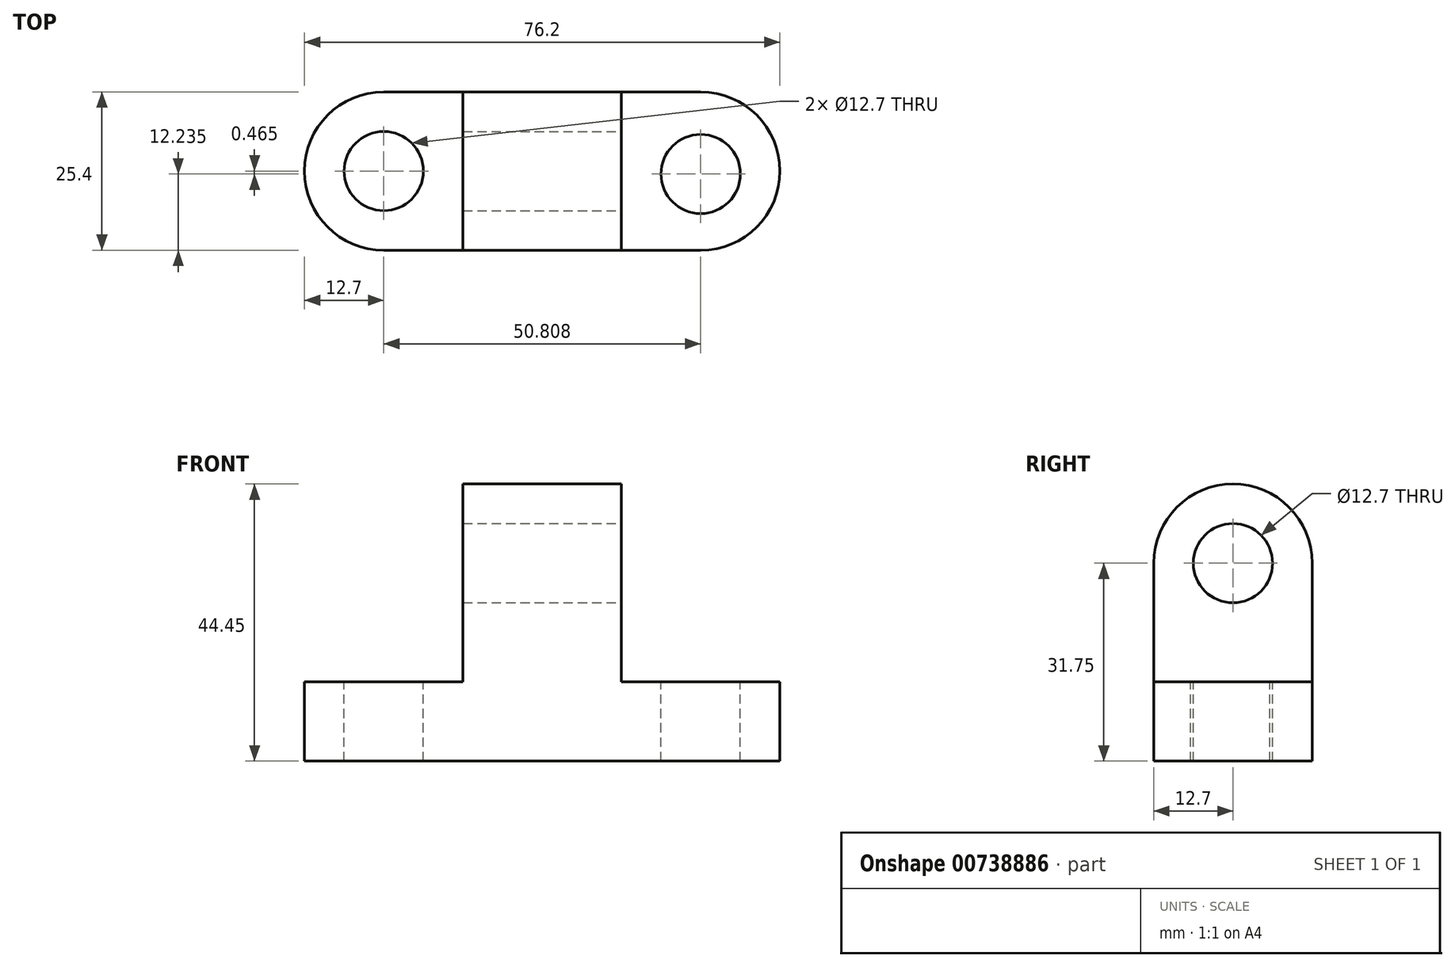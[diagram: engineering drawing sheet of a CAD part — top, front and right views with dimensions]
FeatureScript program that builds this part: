
annotation { "Feature Type Name" : "Feature", "Feature Type Description" : "" }
export const myFeature = defineFeature(function(context is Context, id is Id, definition is map)
    precondition{}
    {
        {
            var Q0;
            Q0=qCreatedBy(makeId("Front.planeOp"),FACE);
            var sketch = newSketch(context, id + "F0", { "sketchPlane" : qUnion([Q0])});
            skLineSegment(sketch, "E0", {"start": v(0, 0) * mm, "end": v(0, 44.45) * mm});
            skLineSegment(sketch, "E1", {"start": v(0, 44.45) * mm, "end": v(76.2, 44.45) * mm});
            skLineSegment(sketch, "E2", {"start": v(76.2, 44.45) * mm, "end": v(76.2, 0) * mm});
            skLineSegment(sketch, "E3", {"start": v(76.2, 0) * mm, "end": v(0, 0) * mm});
            skSolve(sketch);
        }
        {
            var Q0;
            Q0 = qSketchRegion(id + "F0", true);
            extrude(context, id + "F1", {"entities" : qUnion([Q0]), "depth" : 25.4 * mm, "offsetDistance" : 25.4 * mm});
        }
        {
            var Q0;
            Q0=makeQuery(id+"F1.opExtrude","CAP_FACE",FACE,{"disambiguationData":[OSD([sQuery(id+"F0.wireOp",EDGE,"E0"),sQuery(id+"F0.wireOp",EDGE,"E1"),sQuery(id+"F0.wireOp",EDGE,"E2"),sQuery(id+"F0.wireOp",EDGE,"E3")])],"isStart":false});
            var sketch = newSketch(context, id + "F2", { "sketchPlane" : qUnion([Q0])});
            skLineSegment(sketch, "E4", {"start": v(50.8, 44.45) * mm, "end": v(50.8, 12.7) * mm});
            skLineSegment(sketch, "E5", {"start": v(50.8, 12.7) * mm, "end": v(76.2, 12.7) * mm});
            skLineSegment(sketch, "E6", {"start": v(25.4, 44.45) * mm, "end": v(25.4, 12.7) * mm});
            skLineSegment(sketch, "E7", {"start": v(25.4, 12.7) * mm, "end": v(0, 12.7) * mm});
            skSolve(sketch);
        }
        {
            var Q0;
            Q0 = qSketchRegion(id + "F2", true);
            var Q1;
            {var subQ0=sQuery(id+"F2.wireOp",EDGE,"E6");Q1=makeQuery(id+"F2.imprint","IMPRINT",FACE,{"disambiguationData":[TD([[makeQuery(id+"F2.imprint","IMPRINT",EDGE,{"derivedFrom":subQ0}),-1.0]])]});}
            var Q2;
            {var subQ0=sQuery(id+"F2.wireOp",EDGE,"E4");Q2=makeQuery(id+"F2.imprint","IMPRINT",FACE,{"disambiguationData":[TD([[makeQuery(id+"F2.imprint","IMPRINT",EDGE,{"derivedFrom":subQ0}),1.0]])]});}
            extrude(context, id + "F3", {"entities" : qUnion([Q0, Q1, Q2]), "operationType" : NewBodyOperationType.REMOVE, "oppositeDirection" : true, "depth" : 25.4 * mm, "offsetDistance" : 25.4 * mm});
        }
        {
            var Q0;
            Q0=makeQuery(id+"F3.boolean.opBoolean","COPY",FACE,{"derivedFrom":makeQuery(id+"F3.opExtrude","SWEPT_FACE",FACE,{"disambiguationData":[OSD([sQuery(id+"F2.wireOp",EDGE,"E4")])]})});
            var sketch = newSketch(context, id + "F4", { "sketchPlane" : qUnion([Q0])});
            skCircle(sketch, "E8", {"center": v(-12.7, 31.75) * mm, "radius": 6.35 * mm});
            skArc(sketch, "E9", {"start": v(0, 31.75) * mm, "mid": v(-12.7, 44.45) * mm, "end": v(-25.4, 31.75) * mm});
            skSolve(sketch);
        }
        {
            var Q0;
            Q0 = qSketchRegion(id + "F4", true);
            var Q1;
            {var subQ0=sQuery(id+"F4.wireOp",EDGE,"E9");var subQ1=sQuery(id+"F2.wireOp",EDGE,"E4");var subQ2=makeQuery(id+"F3.boolean.opBoolean","COPY",EDGE,{"derivedFrom":makeQuery(id+"F3.opExtrude","CAP_EDGE",EDGE,{"disambiguationData":[OSD([subQ1])],"isStart":false})});var subQ3=makeQuery(id+"F4.imprint","INTERSECT",VERTEX,{"derivedFrom":[subQ2,subQ0]});Q1=makeQuery(id+"F4.imprint","IMPRINT",FACE,{"disambiguationData":[TD([[makeQuery(id+"F4.imprint","IMPRINT",EDGE,{"disambiguationData":[TD([[subQ3,-1.0]])],"derivedFrom":subQ0}),-1.0]])]});}
            var Q2;
            {var subQ0=sQuery(id+"F4.wireOp",EDGE,"E9");var subQ1=sQuery(id+"F2.wireOp",EDGE,"E4");var subQ2=makeQuery(id+"F3.boolean.opBoolean","COPY",EDGE,{"derivedFrom":makeQuery(id+"F3.opExtrude","CAP_EDGE",EDGE,{"disambiguationData":[OSD([subQ1])],"isStart":true})});var subQ3=makeQuery(id+"F4.imprint","INTERSECT",VERTEX,{"derivedFrom":[subQ2,subQ0]});Q2=makeQuery(id+"F4.imprint","IMPRINT",FACE,{"disambiguationData":[TD([[makeQuery(id+"F4.imprint","IMPRINT",EDGE,{"disambiguationData":[TD([[subQ3,1.0]])],"derivedFrom":subQ0}),-1.0]])]});}
            extrude(context, id + "F5", {"entities" : qUnion([Q0, Q1, Q2]), "operationType" : NewBodyOperationType.REMOVE, "oppositeDirection" : true, "depth" : 25.4 * mm, "offsetDistance" : 25.4 * mm});
        }
        {
            var Q0;
            Q0=makeQuery(id+"F3.boolean.opBoolean","COPY",FACE,{"derivedFrom":makeQuery(id+"F3.opExtrude","SWEPT_FACE",FACE,{"disambiguationData":[OSD([sQuery(id+"F2.wireOp",EDGE,"E7")])]})});
            var sketch = newSketch(context, id + "F6", { "sketchPlane" : qUnion([Q0])});
            skCircle(sketch, "E10", {"center": v(12.7, -12.7) * mm, "radius": 6.35 * mm});
            skArc(sketch, "E11", {"start": v(12.7, 0) * mm, "mid": v(0, -12.7) * mm, "end": v(12.7, -25.4) * mm});
            skSolve(sketch);
        }
        {
            var Q0;
            Q0=makeQuery(id+"F6.imprint","IMPRINT",FACE,{"disambiguationData":[TD([[makeQuery(id+"F6.imprint","IMPRINT",EDGE,{"derivedFrom":sQuery(id+"F6.wireOp",EDGE,"E10")}),1.0]])]});
            var Q1;
            {var subQ0=sQuery(id+"F6.wireOp",EDGE,"E11");var subQ1=sQuery(id+"F2.wireOp",EDGE,"E7");var subQ2=makeQuery(id+"F3.boolean.opBoolean","COPY",EDGE,{"derivedFrom":makeQuery(id+"F3.opExtrude","CAP_EDGE",EDGE,{"disambiguationData":[OSD([subQ1])],"isStart":true})});var subQ3=makeQuery(id+"F6.imprint","INTERSECT",VERTEX,{"derivedFrom":[subQ2,subQ0]});Q1=makeQuery(id+"F6.imprint","IMPRINT",FACE,{"disambiguationData":[TD([[makeQuery(id+"F6.imprint","IMPRINT",EDGE,{"disambiguationData":[TD([[subQ3,1.0]])],"derivedFrom":subQ0}),-1.0]])]});}
            var Q2;
            {var subQ0=sQuery(id+"F6.wireOp",EDGE,"E11");var subQ1=sQuery(id+"F2.wireOp",EDGE,"E7");var subQ2=makeQuery(id+"F3.boolean.opBoolean","COPY",EDGE,{"derivedFrom":makeQuery(id+"F3.opExtrude","CAP_EDGE",EDGE,{"disambiguationData":[OSD([subQ1])],"isStart":false})});var subQ3=makeQuery(id+"F6.imprint","INTERSECT",VERTEX,{"derivedFrom":[subQ2,subQ0]});Q2=makeQuery(id+"F6.imprint","IMPRINT",FACE,{"disambiguationData":[TD([[makeQuery(id+"F6.imprint","IMPRINT",EDGE,{"disambiguationData":[TD([[subQ3,-1.0]])],"derivedFrom":subQ0}),-1.0]])]});}
            extrude(context, id + "F7", {"entities" : qUnion([Q0, Q1, Q2]), "operationType" : NewBodyOperationType.REMOVE, "oppositeDirection" : true, "depth" : 25.4 * mm, "offsetDistance" : 25.4 * mm});
        }
        {
            var Q0;
            Q0=makeQuery(id+"F3.boolean.opBoolean","COPY",FACE,{"derivedFrom":makeQuery(id+"F3.opExtrude","SWEPT_FACE",FACE,{"disambiguationData":[OSD([sQuery(id+"F2.wireOp",EDGE,"E5")])]})});
            var sketch = newSketch(context, id + "F8", { "sketchPlane" : qUnion([Q0])});
            skCircle(sketch, "E12", {"center": v(63.5, -13.17) * mm, "radius": 6.35 * mm});
            skArc(sketch, "E13", {"start": v(63.5, -25.4) * mm, "mid": v(76.2, -12.7) * mm, "end": v(63.5, 0) * mm});
            skSolve(sketch);
        }
        {
            var Q0;
            {var subQ0=sQuery(id+"F8.wireOp",EDGE,"E13");var subQ1=sQuery(id+"F2.wireOp",EDGE,"E5");var subQ2=makeQuery(id+"F3.boolean.opBoolean","COPY",EDGE,{"derivedFrom":makeQuery(id+"F3.opExtrude","CAP_EDGE",EDGE,{"disambiguationData":[OSD([subQ1])],"isStart":false})});var subQ3=makeQuery(id+"F8.imprint","INTERSECT",VERTEX,{"derivedFrom":[subQ2,subQ0]});Q0=makeQuery(id+"F8.imprint","IMPRINT",FACE,{"disambiguationData":[TD([[makeQuery(id+"F8.imprint","IMPRINT",EDGE,{"disambiguationData":[TD([[subQ3,1.0]])],"derivedFrom":subQ0}),-1.0]])]});}
            var Q1;
            {var subQ0=sQuery(id+"F8.wireOp",EDGE,"E13");var subQ1=sQuery(id+"F2.wireOp",EDGE,"E5");var subQ2=makeQuery(id+"F3.boolean.opBoolean","COPY",EDGE,{"derivedFrom":makeQuery(id+"F3.opExtrude","CAP_EDGE",EDGE,{"disambiguationData":[OSD([subQ1])],"isStart":true})});var subQ3=makeQuery(id+"F8.imprint","INTERSECT",VERTEX,{"derivedFrom":[subQ2,subQ0]});Q1=makeQuery(id+"F8.imprint","IMPRINT",FACE,{"disambiguationData":[TD([[makeQuery(id+"F8.imprint","IMPRINT",EDGE,{"disambiguationData":[TD([[subQ3,-1.0]])],"derivedFrom":subQ0}),-1.0]])]});}
            var Q2;
            Q2=makeQuery(id+"F8.imprint","IMPRINT",FACE,{"disambiguationData":[TD([[makeQuery(id+"F8.imprint","IMPRINT",EDGE,{"derivedFrom":sQuery(id+"F8.wireOp",EDGE,"E12")}),1.0]])]});
            extrude(context, id + "F9", {"entities" : qUnion([Q0, Q1, Q2]), "operationType" : NewBodyOperationType.REMOVE, "oppositeDirection" : true, "depth" : 25.4 * mm, "offsetDistance" : 25.4 * mm});
        }
    });
